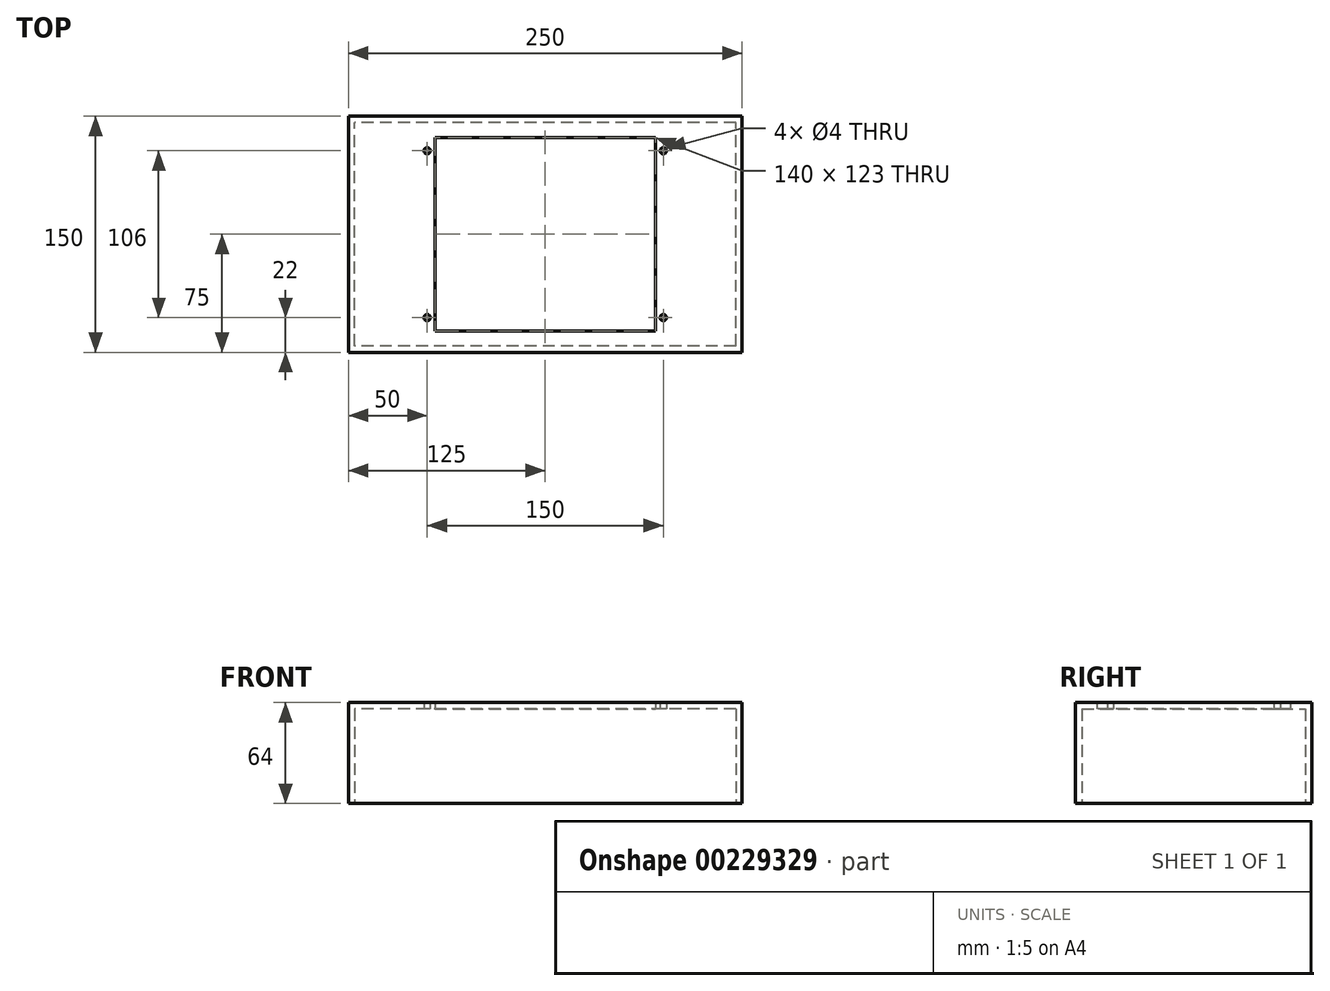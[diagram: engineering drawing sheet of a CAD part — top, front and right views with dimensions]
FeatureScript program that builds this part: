
annotation { "Feature Type Name" : "Feature", "Feature Type Description" : "" }
export const myFeature = defineFeature(function(context is Context, id is Id, definition is map)
    precondition{}
    {
        {
            var Q0;
            Q0=qCreatedBy(makeId("Top.planeOp"),FACE);
            var sketch = newSketch(context, id + "F0", { "sketchPlane" : qUnion([Q0])});
            skLineSegment(sketch, "E0.bottom", {"start": v(125, -75) * mm, "end": v(-125, -75) * mm});
            skLineSegment(sketch, "E0.top", {"start": v(125, 75) * mm, "end": v(-125, 75) * mm});
            skLineSegment(sketch, "E0.left", {"start": v(125, -75) * mm, "end": v(125, 75) * mm});
            skLineSegment(sketch, "E0.right", {"start": v(-125, -75) * mm, "end": v(-125, 75) * mm});
            skPoint(sketch, "E0.middle", {"position": v(0, 0) * mm});
            skSolve(sketch);
        }
        {
            var Q0;
            Q0=makeQuery(id+"F0.imprint","IMPRINT",FACE,{"disambiguationData":[TD([[makeQuery(id+"F0.imprint","IMPRINT",EDGE,{"derivedFrom":sQuery(id+"F0.wireOp",EDGE,"E0.bottom")}),-1.0]])]});
            extrude(context, id + "F1", {"entities" : qUnion([Q0]), "depth" : 64 * mm});
        }
        {
            var Q0;
            Q0=makeQuery(id+"F1.opExtrude","CAP_FACE",FACE,{"disambiguationData":[OSD([sQuery(id+"F0.wireOp",EDGE,"E0.bottom"),sQuery(id+"F0.wireOp",EDGE,"E0.top"),sQuery(id+"F0.wireOp",EDGE,"E0.left"),sQuery(id+"F0.wireOp",EDGE,"E0.right")])],"isStart":true});
            shell(context, id + "F2", {"entities" : qUnion([Q0]), "thickness" : 4 * mm});
        }
        {
            var Q0;
            Q0=qCreatedBy(makeId("Top.planeOp"),FACE);
            var sketch = newSketch(context, id + "F3", { "sketchPlane" : qUnion([Q0])});
            skLineSegment(sketch, "E1.bottom", {"start": v(70, -61.5) * mm, "end": v(-70, -61.5) * mm});
            skLineSegment(sketch, "E1.top", {"start": v(70, 61.5) * mm, "end": v(-70, 61.5) * mm});
            skLineSegment(sketch, "E1.left", {"start": v(70, -61.5) * mm, "end": v(70, 61.5) * mm});
            skLineSegment(sketch, "E1.right", {"start": v(-70, -61.5) * mm, "end": v(-70, 61.5) * mm});
            skPoint(sketch, "E1.middle", {"position": v(0, 0) * mm});
            skCircle(sketch, "E2", {"center": v(-75, -53) * mm, "radius": 2 * mm});
            skCircle(sketch, "E3.MirrorC", {"center": v(75, -53) * mm, "radius": 2 * mm});
            skCircle(sketch, "E4.MirrorC", {"center": v(-75, 53) * mm, "radius": 2 * mm});
            skCircle(sketch, "E5.MirrorC", {"center": v(75, 53) * mm, "radius": 2 * mm});
            skSolve(sketch);
        }
        {
            var Q0;
            Q0 = qSketchRegion(id + "F3", true);
            extrude(context, id + "F4", {"entities" : qUnion([Q0]), "operationType" : NewBodyOperationType.REMOVE, "endBound" : BoundingType.THROUGH_ALL, "depth" : 25 * mm});
        }
    });
